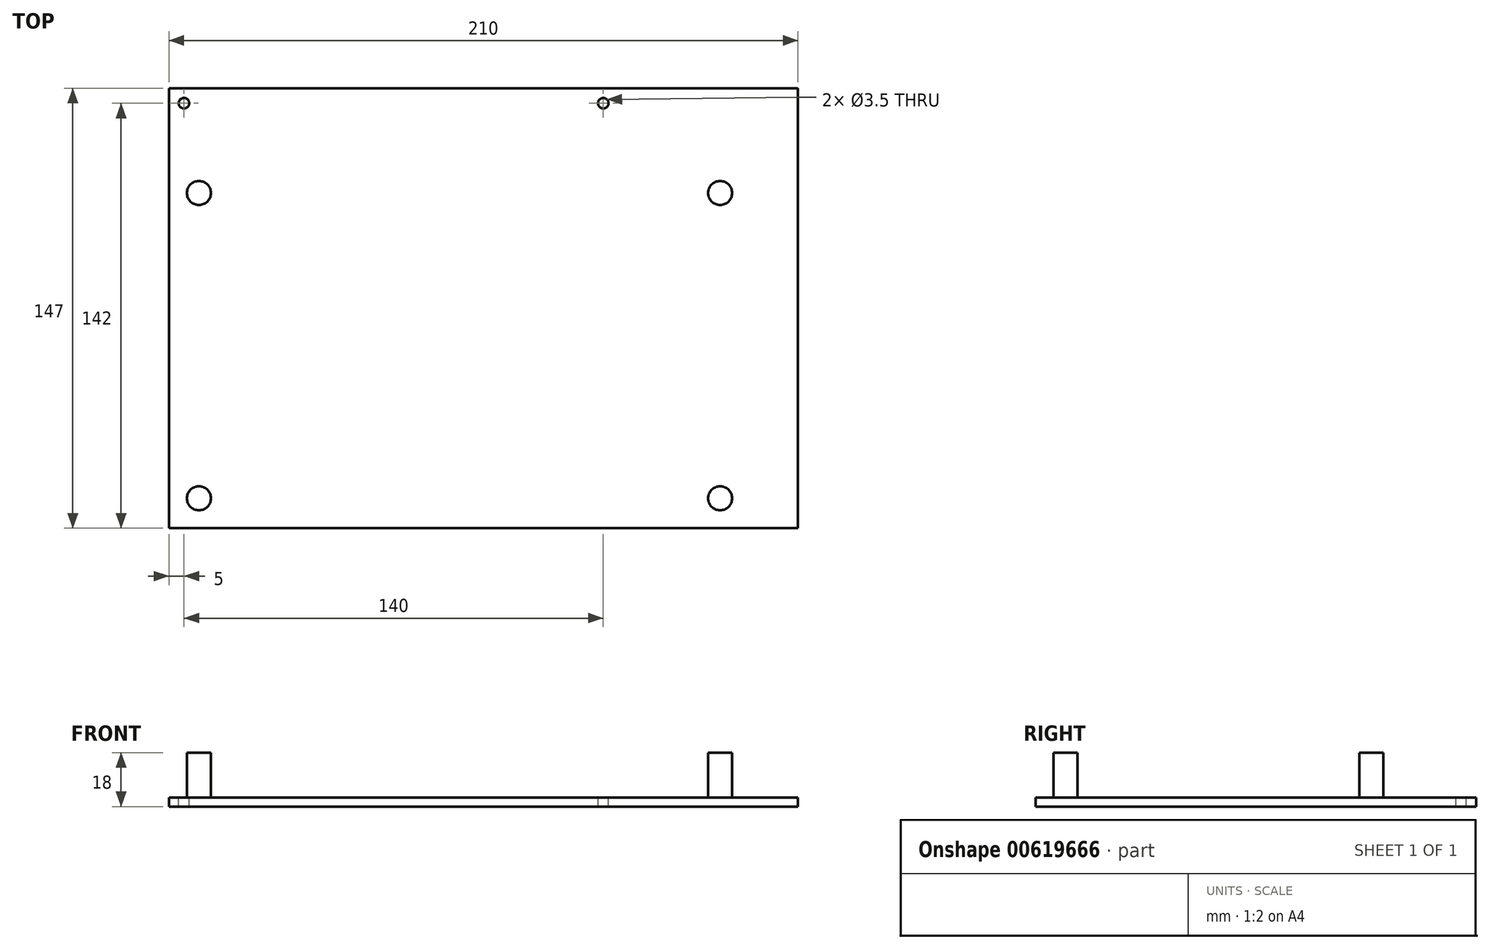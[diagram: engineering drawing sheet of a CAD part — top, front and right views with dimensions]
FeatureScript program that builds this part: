
annotation { "Feature Type Name" : "Feature", "Feature Type Description" : "" }
export const myFeature = defineFeature(function(context is Context, id is Id, definition is map)
    precondition{}
    {
        {
            var Q0;
            Q0=qCreatedBy(makeId("Top.planeOp"),FACE);
            var sketch = newSketch(context, id + "F0", { "sketchPlane" : qUnion([Q0])});
            skLineSegment(sketch, "E0.bottom", {"start": v(0, 0) * mm, "end": v(210, 0) * mm});
            skLineSegment(sketch, "E0.top", {"start": v(0, -147) * mm, "end": v(210, -147) * mm});
            skLineSegment(sketch, "E0.left", {"start": v(0, 0) * mm, "end": v(0, -147) * mm});
            skLineSegment(sketch, "E0.right", {"start": v(210, 0) * mm, "end": v(210, -147) * mm});
            skSolve(sketch);
        }
        {
            var Q0;
            Q0=makeQuery(id+"F0.imprint","IMPRINT",FACE,{"disambiguationData":[TD([[makeQuery(id+"F0.imprint","IMPRINT",EDGE,{"derivedFrom":sQuery(id+"F0.wireOp",EDGE,"E0.bottom")}),-1.0]])]});
            extrude(context, id + "F1", {"entities" : qUnion([Q0]), "depth" : 3 * mm, "offsetDistance" : 25 * mm});
        }
        {
            var Q0;
            Q0=makeQuery(id+"F1.opExtrude","CAP_FACE",FACE,{"disambiguationData":[OSD([sQuery(id+"F0.wireOp",EDGE,"E0.bottom"),sQuery(id+"F0.wireOp",EDGE,"E0.top"),sQuery(id+"F0.wireOp",EDGE,"E0.left"),sQuery(id+"F0.wireOp",EDGE,"E0.right")])],"isStart":false});
            var sketch = newSketch(context, id + "F2", { "sketchPlane" : qUnion([Q0])});
            skLineSegment(sketch, "E1", {"start": v(0, -5) * mm, "end": v(210, -5) * mm, "construction": true});
            skCircle(sketch, "E2", {"center": v(5, -5) * mm, "radius": 1.75 * mm});
            skCircle(sketch, "E3", {"center": v(145, -5) * mm, "radius": 1.75 * mm});
            skLineSegment(sketch, "E4", {"start": v(0, -35) * mm, "end": v(210, -35) * mm, "construction": true});
            skLineSegment(sketch, "E5", {"start": v(0, -137) * mm, "end": v(210, -137) * mm, "construction": true});
            skCircle(sketch, "E6", {"center": v(10, -35) * mm, "radius": 4 * mm});
            skCircle(sketch, "E7", {"center": v(184, -35) * mm, "radius": 4 * mm});
            skCircle(sketch, "E8", {"center": v(10, -137) * mm, "radius": 4 * mm});
            skCircle(sketch, "E9", {"center": v(184, -137) * mm, "radius": 4 * mm});
            skSolve(sketch);
        }
        {
            var Q0;
            Q0=makeQuery(id+"F2.imprint","IMPRINT",FACE,{"disambiguationData":[TD([[makeQuery(id+"F2.imprint","IMPRINT",EDGE,{"derivedFrom":sQuery(id+"F2.wireOp",EDGE,"E6")}),1.0]])]});
            var Q1;
            Q1=makeQuery(id+"F2.imprint","IMPRINT",FACE,{"disambiguationData":[TD([[makeQuery(id+"F2.imprint","IMPRINT",EDGE,{"derivedFrom":sQuery(id+"F2.wireOp",EDGE,"E7")}),1.0]])]});
            var Q2;
            Q2=makeQuery(id+"F2.imprint","IMPRINT",FACE,{"disambiguationData":[TD([[makeQuery(id+"F2.imprint","IMPRINT",EDGE,{"derivedFrom":sQuery(id+"F2.wireOp",EDGE,"E9")}),1.0]])]});
            var Q3;
            Q3=makeQuery(id+"F2.imprint","IMPRINT",FACE,{"disambiguationData":[TD([[makeQuery(id+"F2.imprint","IMPRINT",EDGE,{"derivedFrom":sQuery(id+"F2.wireOp",EDGE,"E8")}),1.0]])]});
            extrude(context, id + "F3", {"entities" : qUnion([Q0, Q1, Q2, Q3]), "operationType" : NewBodyOperationType.ADD, "depth" : 15 * mm, "offsetDistance" : 25 * mm});
        }
        {
            var Q0;
            Q0=makeQuery(id+"F1.opExtrude","CAP_FACE",FACE,{"disambiguationData":[OSD([sQuery(id+"F0.wireOp",EDGE,"E0.bottom"),sQuery(id+"F0.wireOp",EDGE,"E0.top"),sQuery(id+"F0.wireOp",EDGE,"E0.left"),sQuery(id+"F0.wireOp",EDGE,"E0.right")])],"isStart":false});
            var sketch = newSketch(context, id + "F4", { "sketchPlane" : qUnion([Q0])});
            skLineSegment(sketch, "E10", {"start": v(0, -5) * mm, "end": v(210, -5) * mm, "construction": true});
            skCircle(sketch, "E11", {"center": v(5, -5) * mm, "radius": 1.75 * mm});
            skCircle(sketch, "E12", {"center": v(145, -5) * mm, "radius": 1.75 * mm});
            skSolve(sketch);
        }
        {
            var Q0;
            Q0=makeQuery(id+"F4.imprint","IMPRINT",FACE,{"disambiguationData":[TD([[makeQuery(id+"F4.imprint","IMPRINT",EDGE,{"derivedFrom":sQuery(id+"F4.wireOp",EDGE,"E11")}),1.0]])]});
            var Q1;
            Q1=makeQuery(id+"F4.imprint","IMPRINT",FACE,{"disambiguationData":[TD([[makeQuery(id+"F4.imprint","IMPRINT",EDGE,{"derivedFrom":sQuery(id+"F4.wireOp",EDGE,"E12")}),1.0]])]});
            extrude(context, id + "F5", {"entities" : qUnion([Q0, Q1]), "operationType" : NewBodyOperationType.REMOVE, "oppositeDirection" : true, "depth" : 25 * mm, "offsetDistance" : 25 * mm});
        }
    });
